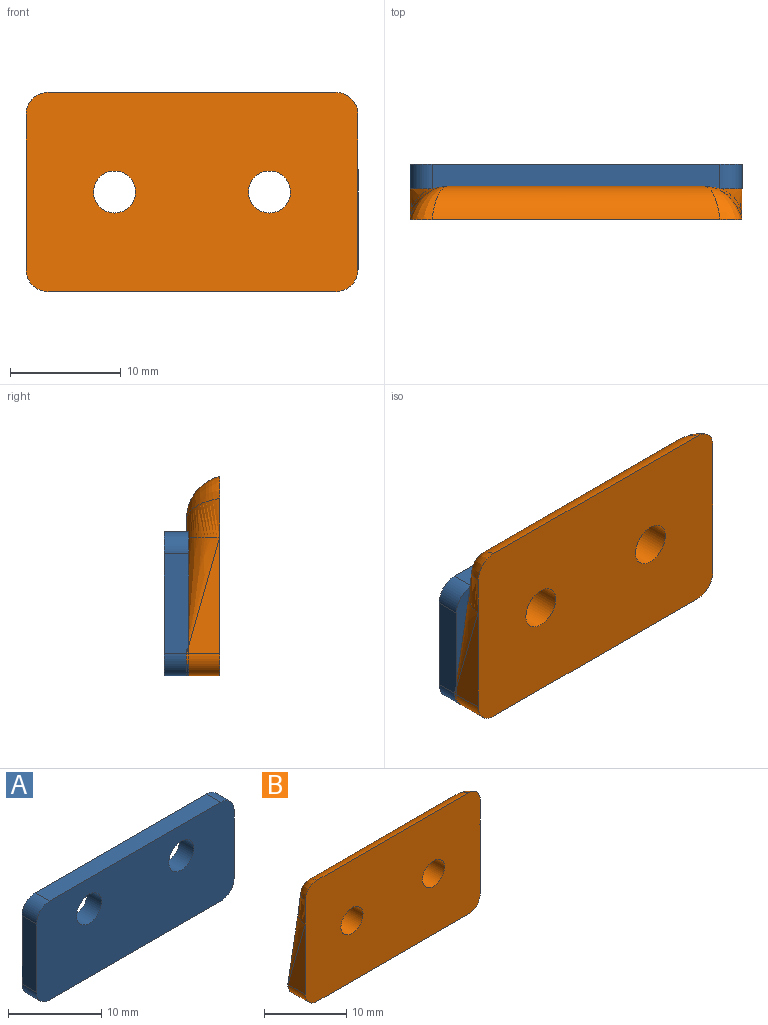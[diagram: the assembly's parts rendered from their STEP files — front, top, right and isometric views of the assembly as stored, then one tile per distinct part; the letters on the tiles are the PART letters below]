
ASSEMBLY  parts=2 mates=1
PART A: 12 faces, bbox 30x2.2x13 mm
  f0: plane 26x2.2mm, normal (0,0,1), area 57.2mm2, adj f6,f7,f8,f11
  f1: plane 9x2.2mm, normal (-1,0,0), area 19.8mm2, adj f6,f7,f8,f9
  f2: plane 26x2.2mm, normal (0,0,-1), area 57.2mm2, adj f6,f7,f9,f10
  f3: cylinder r=1.9mm len=3.8mm, axis (0,1,0), area 26.3mm2, adj f6,f7
  f4: cylinder r=1.9mm len=3.8mm, axis (0,1,0), area 26.3mm2, adj f6,f7
  f5: plane 9x2.2mm, normal (1,0,0), area 19.8mm2, adj f6,f7,f10,f11
  f6: plane 30x13mm, normal (0,-1,0), area 363.9mm2, adj f0,f1,f2,f3,f4,f5,f8,f9
  f7: plane 30x13mm, normal (0,1,0), area 363.9mm2, adj f0,f1,f2,f3,f4,f5,f8,f9
  f8: cylinder r=2mm len=2.2mm, axis (0,-1,0), area 6.9mm2, adj f0,f1,f6,f7
  f9: cylinder r=2mm len=2.2mm, axis (0,1,0), area 6.9mm2, adj f1,f2,f6,f7
  f10: cylinder r=2mm len=2.2mm, axis (0,-1,0), area 6.9mm2, adj f2,f5,f6,f7
  f11: cylinder r=2mm len=2.2mm, axis (0,1,0), area 6.9mm2, adj f0,f5,f6,f7
PART B: 16 faces, bbox 31.2x5.2x19.2 mm
  f0: plane 26x3mm, normal (0,0,-1), area 78mm2, adj f1,f6,f7,f8
  f1: cylinder r=2mm len=3mm, axis (0,1,0), area 9.4mm2, adj f0,f2,f7,f8
  f2: plane 11.6x4.1mm, normal (1,0,0), area 15.7mm2, adj f1,f7,f14
  f3: plane 11.65x4.15mm, normal (-1,0,0), area 15.7mm2, adj f6,f7,f9
  f4: cylinder r=1.9mm len=3.8mm, axis (0,1,0), area 35.8mm2, adj f7,f8
  f5: cylinder r=1.9mm len=3.8mm, axis (0,1,0), area 35.8mm2, adj f7,f8
  f6: cylinder r=2mm len=3mm, axis (0,1,0), area 9.4mm2, adj f0,f3,f7,f8
  f7: plane 30x18mm, normal (0,-1,0), area 513.9mm2, adj f0,f1,f2,f3,f4,f5,f6,f10
  f8: plane 31.15x15.29mm, normal (0,1,0), area 357.4mm2, adj f0,f1,f4,f5,f6,f9,f10,f12
  f9: bspline ~14x4mm, area 16.9mm2, adj f3,f8,f10
  f10: bspline ~3.91x3.62mm, area 12.7mm2, adj f7,f8,f9,f11
  f11: bspline ~3.87x3.43mm, area 6.4mm2, adj f7,f10,f12
  f12: cylinder r=4mm len=26mm, axis (1,0,0), area 129.5mm2, adj f7,f8,f11,f13
  f13: bspline ~3.87x3.43mm, area 9.8mm2, adj f7,f12,f15
  f14: bspline ~14x4mm, area 16.9mm2, adj f2,f8,f15
  f15: bspline ~3.87x3.5mm, area 12.7mm2, adj f7,f8,f13,f14
PLACE A t=(108,23.25,-18.39)mm
PLACE B t=(33.35,21.25,-5.81)mm
MATE parallel A.f6 <-> B.f8  axis (0,-1,0) through (73.31,21.05,7.91)mm
